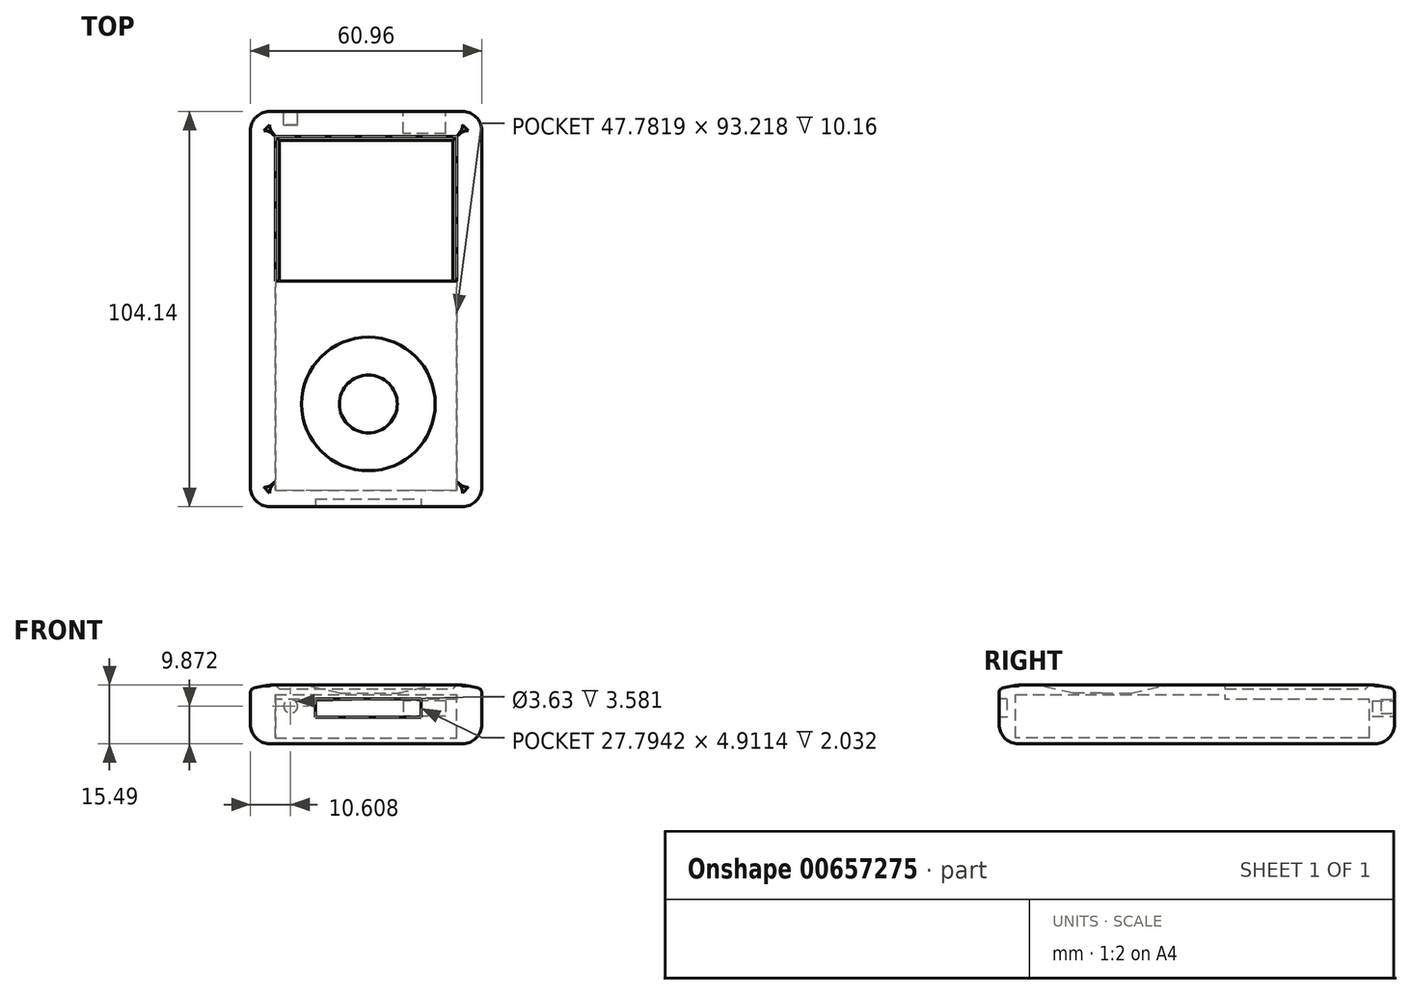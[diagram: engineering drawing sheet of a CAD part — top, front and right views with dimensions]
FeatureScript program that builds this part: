
annotation { "Feature Type Name" : "Feature", "Feature Type Description" : "" }
export const myFeature = defineFeature(function(context is Context, id is Id, definition is map)
    precondition{}
    {
        {
            var Q0;
            Q0=qCreatedBy(makeId("Top.planeOp"),FACE);
            var sketch = newSketch(context, id + "F0", { "sketchPlane" : qUnion([Q0])});
            skLineSegment(sketch, "E0.bottom", {"start": v(-31.08, 69.47) * mm, "end": v(29.88, 69.47) * mm});
            skLineSegment(sketch, "E0.top", {"start": v(-31.08, -34.67) * mm, "end": v(29.88, -34.67) * mm});
            skLineSegment(sketch, "E0.left", {"start": v(-31.08, 69.47) * mm, "end": v(-31.08, -34.67) * mm});
            skLineSegment(sketch, "E0.right", {"start": v(29.88, 69.47) * mm, "end": v(29.88, -34.67) * mm});
            skSolve(sketch);
        }
        {
            var Q0;
            Q0=makeQuery(id+"F0.imprint","IMPRINT",FACE,{"disambiguationData":[TD([[makeQuery(id+"F0.imprint","IMPRINT",EDGE,{"derivedFrom":sQuery(id+"F0.wireOp",EDGE,"E0.bottom")}),-1.0]])]});
            extrude(context, id + "F1", {"entities" : qUnion([Q0]), "depth" : 15.24 * mm, "offsetDistance" : 25.4 * mm});
        }
        {
            var Q0;
            Q0=makeQuery(id+"F1.opExtrude","SWEPT_EDGE",EDGE,{"disambiguationData":[OSD([sQuery(id+"F0.wireOp",EDGE,"E0.bottom"),sQuery(id+"F0.wireOp",EDGE,"E0.right")])]});
            var Q1;
            Q1=makeQuery(id+"F1.opExtrude","SWEPT_EDGE",EDGE,{"disambiguationData":[OSD([sQuery(id+"F0.wireOp",EDGE,"E0.bottom"),sQuery(id+"F0.wireOp",EDGE,"E0.left")])]});
            var Q2;
            Q2=makeQuery(id+"F1.opExtrude","SWEPT_EDGE",EDGE,{"disambiguationData":[OSD([sQuery(id+"F0.wireOp",EDGE,"E0.top"),sQuery(id+"F0.wireOp",EDGE,"E0.right")])]});
            var Q3;
            Q3=makeQuery(id+"F1.opExtrude","SWEPT_EDGE",EDGE,{"disambiguationData":[OSD([sQuery(id+"F0.wireOp",EDGE,"E0.top"),sQuery(id+"F0.wireOp",EDGE,"E0.left")])]});
            fillet(context, id + "F2", {"entities" : qUnion([Q0, Q1, Q2, Q3]), "radius" : 5.08 * mm, "tangentPropagation" : true, "allowEdgeOverflow" : false});
        }
        {
            var Q0;
            Q0=makeQuery(id+"FoFVW0M2sbFO0MS_1.boolean.opBoolean","SPLIT",FACE,{"disambiguationData":[TD([makeQuery(id+"FoFVW0M2sbFO0MS_1.opExtrude","SWEPT_FACE",FACE,{"disambiguationData":[OSD([sQuery(id+"FxMzDEaBXAed3TF_1.wireOp",EDGE,"OPwGTAcq-u0Vr-5pPN-neVn-fGhoZMYUlgc0")])]})])],"derivedFrom":makeQuery(id+"F1.opExtrude","CAP_FACE",FACE,{"disambiguationData":[OSD([sQuery(id+"F0.wireOp",EDGE,"E0.bottom"),sQuery(id+"F0.wireOp",EDGE,"E0.top"),sQuery(id+"F0.wireOp",EDGE,"E0.left"),sQuery(id+"F0.wireOp",EDGE,"E0.right")])],"isStart":false})});
            extrude(context, id + "F3", {"entities" : qUnion([Q0]), "operationType" : NewBodyOperationType.ADD, "depth" : 0.25 * mm, "offsetDistance" : 25.4 * mm});
        }
        {
            var Q0;
            Q0=makeQuery(id+"F1.opExtrude","CAP_EDGE",EDGE,{"disambiguationData":[OSD([sQuery(id+"F0.wireOp",EDGE,"E0.right")])],"isStart":true});
            var Q1;
            Q1=makeQuery(id+"F1.opExtrude","CAP_EDGE",EDGE,{"disambiguationData":[OSD([sQuery(id+"F0.wireOp",EDGE,"E0.bottom")])],"isStart":true});
            var Q2;
            Q2=makeQuery(id+"F1.opExtrude","CAP_EDGE",EDGE,{"disambiguationData":[OSD([sQuery(id+"F0.wireOp",EDGE,"E0.left")])],"isStart":true});
            var Q3;
            Q3=makeQuery(id+"F1.opExtrude","CAP_EDGE",EDGE,{"disambiguationData":[OSD([sQuery(id+"F0.wireOp",EDGE,"E0.top")])],"isStart":true});
            var Q4;
            {var subQ0=sQuery(id+"F0.wireOp",EDGE,"E0.left");var subQ1=sQuery(id+"F0.wireOp",EDGE,"E0.top");Q4=makeQuery(id+"F2.opFillet","BLEND_EDGE",EDGE,{"blendedFrom":[makeQuery(id+"F1.opExtrude","SWEPT_EDGE",EDGE,{"disambiguationData":[OSD([subQ1,subQ0])]}),makeQuery(id+"F1.opExtrude","CAP_FACE",FACE,{"disambiguationData":[OSD([sQuery(id+"F0.wireOp",EDGE,"E0.bottom"),subQ1,subQ0,sQuery(id+"F0.wireOp",EDGE,"E0.right")])],"isStart":true})],"blendedInto":[makeQuery(id+"F1.opExtrude","CAP_FACE",FACE,{"disambiguationData":[OSD([sQuery(id+"F0.wireOp",EDGE,"E0.bottom"),subQ1,subQ0,sQuery(id+"F0.wireOp",EDGE,"E0.right")])],"isStart":true})]});}
            var Q5;
            {var subQ0=sQuery(id+"F0.wireOp",EDGE,"E0.right");var subQ1=sQuery(id+"F0.wireOp",EDGE,"E0.top");Q5=makeQuery(id+"F2.opFillet","BLEND_EDGE",EDGE,{"blendedFrom":[makeQuery(id+"F1.opExtrude","SWEPT_EDGE",EDGE,{"disambiguationData":[OSD([subQ1,subQ0])]}),makeQuery(id+"F1.opExtrude","CAP_FACE",FACE,{"disambiguationData":[OSD([sQuery(id+"F0.wireOp",EDGE,"E0.bottom"),subQ1,sQuery(id+"F0.wireOp",EDGE,"E0.left"),subQ0])],"isStart":true})],"blendedInto":[makeQuery(id+"F1.opExtrude","CAP_FACE",FACE,{"disambiguationData":[OSD([sQuery(id+"F0.wireOp",EDGE,"E0.bottom"),subQ1,sQuery(id+"F0.wireOp",EDGE,"E0.left"),subQ0])],"isStart":true})]});}
            var Q6;
            {var subQ0=sQuery(id+"F0.wireOp",EDGE,"E0.left");var subQ1=sQuery(id+"F0.wireOp",EDGE,"E0.bottom");Q6=makeQuery(id+"F2.opFillet","BLEND_EDGE",EDGE,{"blendedFrom":[makeQuery(id+"F1.opExtrude","SWEPT_EDGE",EDGE,{"disambiguationData":[OSD([subQ1,subQ0])]}),makeQuery(id+"F1.opExtrude","CAP_FACE",FACE,{"disambiguationData":[OSD([subQ1,sQuery(id+"F0.wireOp",EDGE,"E0.top"),subQ0,sQuery(id+"F0.wireOp",EDGE,"E0.right")])],"isStart":true})],"blendedInto":[makeQuery(id+"F1.opExtrude","CAP_FACE",FACE,{"disambiguationData":[OSD([subQ1,sQuery(id+"F0.wireOp",EDGE,"E0.top"),subQ0,sQuery(id+"F0.wireOp",EDGE,"E0.right")])],"isStart":true})]});}
            var Q7;
            {var subQ0=sQuery(id+"F0.wireOp",EDGE,"E0.right");var subQ1=sQuery(id+"F0.wireOp",EDGE,"E0.bottom");Q7=makeQuery(id+"F2.opFillet","BLEND_EDGE",EDGE,{"blendedFrom":[makeQuery(id+"F1.opExtrude","SWEPT_EDGE",EDGE,{"disambiguationData":[OSD([subQ1,subQ0])]}),makeQuery(id+"F1.opExtrude","CAP_FACE",FACE,{"disambiguationData":[OSD([subQ1,sQuery(id+"F0.wireOp",EDGE,"E0.top"),sQuery(id+"F0.wireOp",EDGE,"E0.left"),subQ0])],"isStart":true})],"blendedInto":[makeQuery(id+"F1.opExtrude","CAP_FACE",FACE,{"disambiguationData":[OSD([subQ1,sQuery(id+"F0.wireOp",EDGE,"E0.top"),sQuery(id+"F0.wireOp",EDGE,"E0.left"),subQ0])],"isStart":true})]});}
            fillet(context, id + "F4", {"entities" : qUnion([Q0, Q1, Q2, Q3, Q4, Q5, Q6, Q7]), "radius" : 5.08 * mm, "tangentPropagation" : true, "allowEdgeOverflow" : false});
        }
        {
            var Q0;
            Q0=qCreatedBy(makeId("Right.planeOp"),FACE);
            var sketch = newSketch(context, id + "F5", { "sketchPlane" : qUnion([Q0])});
            skLineSegment(sketch, "E1", {"start": v(-7.62, 15.53) * mm, "end": v(-7.62, 13.3) * mm});
            skLineSegment(sketch, "E2", {"start": v(-7.62, 13.3) * mm, "end": v(0, 13.3) * mm});
            skLineSegment(sketch, "E3", {"start": v(0, 13.3) * mm, "end": v(10.16, 15.53) * mm});
            skLineSegment(sketch, "E4", {"start": v(10.16, 15.53) * mm, "end": v(-7.62, 15.53) * mm});
            skSolve(sketch);
        }
        {
            var Q0;
            Q0 = qSketchRegion(id + "F5", true);
            var Q1;
            Q1=sQuery(id+"F5.wireOp",EDGE,"E1");
            revolve(context, id + "F6", {"operationType" : NewBodyOperationType.REMOVE, "entities" : qUnion([Q0]), "axis" : qUnion([Q1]), "revolveType" : RevolveType.FULL, "oppositeDirection" : true});
        }
        {
            var Q0;
            Q0=makeQuery(id+"F3.opExtrude","CAP_EDGE",EDGE,{"disambiguationData":[OSD([sQuery(id+"F0.wireOp",EDGE,"E0.left")])],"isStart":false});
            chamfer(context, id + "F7", {"entities" : qUnion([Q0]), "chamferType" : ChamferType.TWO_OFFSETS, "width1" : 5.08 * mm, "oppositeDirection" : false, "width2" : 1.02 * mm, "tangentPropagation" : true});
        }
        {
            var Q0;
            {var subQ0=sQuery(id+"F0.wireOp",EDGE,"E0.left");Q0=makeQuery(id+"F7.opChamfer","BLEND_EDGE",EDGE,{"blendedFrom":[makeQuery(id+"F3.opExtrude","CAP_EDGE",EDGE,{"disambiguationData":[OSD([subQ0])],"isStart":false}),makeQuery(id+"F3.opExtrude","CAP_FACE",FACE,{"disambiguationData":[OSD([sQuery(id+"F0.wireOp",EDGE,"E0.bottom"),sQuery(id+"F0.wireOp",EDGE,"E0.top"),subQ0,sQuery(id+"F0.wireOp",EDGE,"E0.right")])],"isStart":false})],"blendedInto":[makeQuery(id+"F3.opExtrude","CAP_FACE",FACE,{"disambiguationData":[OSD([sQuery(id+"F0.wireOp",EDGE,"E0.bottom"),sQuery(id+"F0.wireOp",EDGE,"E0.top"),subQ0,sQuery(id+"F0.wireOp",EDGE,"E0.right")])],"isStart":false})]});}
            var Q1;
            {var subQ0=sQuery(id+"F0.wireOp",EDGE,"E0.top");Q1=makeQuery(id+"F7.opChamfer","BLEND_EDGE",EDGE,{"blendedFrom":[makeQuery(id+"F3.opExtrude","CAP_EDGE",EDGE,{"disambiguationData":[OSD([subQ0])],"isStart":false}),makeQuery(id+"F3.opExtrude","CAP_FACE",FACE,{"disambiguationData":[OSD([sQuery(id+"F0.wireOp",EDGE,"E0.bottom"),subQ0,sQuery(id+"F0.wireOp",EDGE,"E0.left"),sQuery(id+"F0.wireOp",EDGE,"E0.right")])],"isStart":false})],"blendedInto":[makeQuery(id+"F3.opExtrude","CAP_FACE",FACE,{"disambiguationData":[OSD([sQuery(id+"F0.wireOp",EDGE,"E0.bottom"),subQ0,sQuery(id+"F0.wireOp",EDGE,"E0.left"),sQuery(id+"F0.wireOp",EDGE,"E0.right")])],"isStart":false})]});}
            var Q2;
            {var subQ0=sQuery(id+"F0.wireOp",EDGE,"E0.right");Q2=makeQuery(id+"F7.opChamfer","BLEND_EDGE",EDGE,{"blendedFrom":[makeQuery(id+"F3.opExtrude","CAP_EDGE",EDGE,{"disambiguationData":[OSD([subQ0])],"isStart":false}),makeQuery(id+"F3.opExtrude","CAP_FACE",FACE,{"disambiguationData":[OSD([sQuery(id+"F0.wireOp",EDGE,"E0.bottom"),sQuery(id+"F0.wireOp",EDGE,"E0.top"),sQuery(id+"F0.wireOp",EDGE,"E0.left"),subQ0])],"isStart":false})],"blendedInto":[makeQuery(id+"F3.opExtrude","CAP_FACE",FACE,{"disambiguationData":[OSD([sQuery(id+"F0.wireOp",EDGE,"E0.bottom"),sQuery(id+"F0.wireOp",EDGE,"E0.top"),sQuery(id+"F0.wireOp",EDGE,"E0.left"),subQ0])],"isStart":false})]});}
            var Q3;
            {var subQ0=sQuery(id+"F0.wireOp",EDGE,"E0.bottom");Q3=makeQuery(id+"F7.opChamfer","BLEND_EDGE",EDGE,{"blendedFrom":[makeQuery(id+"F3.opExtrude","CAP_EDGE",EDGE,{"disambiguationData":[OSD([subQ0])],"isStart":false}),makeQuery(id+"F3.opExtrude","CAP_FACE",FACE,{"disambiguationData":[OSD([subQ0,sQuery(id+"F0.wireOp",EDGE,"E0.top"),sQuery(id+"F0.wireOp",EDGE,"E0.left"),sQuery(id+"F0.wireOp",EDGE,"E0.right")])],"isStart":false})],"blendedInto":[makeQuery(id+"F3.opExtrude","CAP_FACE",FACE,{"disambiguationData":[OSD([subQ0,sQuery(id+"F0.wireOp",EDGE,"E0.top"),sQuery(id+"F0.wireOp",EDGE,"E0.left"),sQuery(id+"F0.wireOp",EDGE,"E0.right")])],"isStart":false})]});}
            fillet(context, id + "F8", {"entities" : qUnion([Q0, Q1, Q2, Q3]), "radius" : 15.24 * mm, "tangentPropagation" : true, "allowEdgeOverflow" : false});
        }
        {
            var Q0;
            Q0=makeQuery(id+"F3.opExtrude","CAP_FACE",FACE,{"disambiguationData":[OSD([sQuery(id+"F0.wireOp",EDGE,"E0.bottom"),sQuery(id+"F0.wireOp",EDGE,"E0.top"),sQuery(id+"F0.wireOp",EDGE,"E0.left"),sQuery(id+"F0.wireOp",EDGE,"E0.right")])],"isStart":false});
            var sketch = newSketch(context, id + "F9", { "sketchPlane" : qUnion([Q0])});
            skLineSegment(sketch, "E5.bottom", {"start": v(-24.5, 62.88) * mm, "end": v(23.29, 62.88) * mm});
            skLineSegment(sketch, "E5.top", {"start": v(-24.5, 24.78) * mm, "end": v(23.29, 24.78) * mm});
            skLineSegment(sketch, "E5.left", {"start": v(-24.5, 62.88) * mm, "end": v(-24.5, 24.78) * mm});
            skLineSegment(sketch, "E5.right", {"start": v(23.29, 62.88) * mm, "end": v(23.29, 24.78) * mm});
            skSolve(sketch);
        }
        {
            var Q0;
            Q0 = qSketchRegion(id + "F9", true);
            extrude(context, id + "F10", {"entities" : qUnion([Q0]), "operationType" : NewBodyOperationType.REMOVE, "oppositeDirection" : true, "depth" : 13.97 * mm, "offsetDistance" : 25.4 * mm});
        }
        {
            var Q0;
            Q0=makeQuery(id+"F10.boolean.opBoolean","COPY",FACE,{"derivedFrom":makeQuery(id+"F10.opExtrude","SWEPT_FACE",FACE,{"disambiguationData":[OSD([sQuery(id+"F9.wireOp",EDGE,"E5.top")])]})});
            var sketch = newSketch(context, id + "F11", { "sketchPlane" : qUnion([Q0])});
            skLineSegment(sketch, "E6.0", {"start": v(24.5, 1.52) * mm, "end": v(-23.29, 1.52) * mm});
            skLineSegment(sketch, "E7", {"start": v(-23.29, 1.52) * mm, "end": v(-23.29, 12.95) * mm});
            skLineSegment(sketch, "E8", {"start": v(-23.29, 12.95) * mm, "end": v(24.5, 12.95) * mm});
            skLineSegment(sketch, "E9", {"start": v(24.5, 12.95) * mm, "end": v(24.5, 1.52) * mm});
            skSolve(sketch);
        }
        {
            var Q0;
            Q0=makeQuery(id+"F11.imprint","IMPRINT",FACE,{"disambiguationData":[TD([[makeQuery(id+"F11.imprint","IMPRINT",EDGE,{"derivedFrom":sQuery(id+"F11.wireOp",EDGE,"E6.0")}),-1.0]])]});
            extrude(context, id + "F12", {"entities" : qUnion([Q0]), "operationType" : NewBodyOperationType.REMOVE, "oppositeDirection" : true, "depth" : 55.12 * mm, "offsetDistance" : 25.4 * mm});
        }
        {
            var Q0;
            Q0=makeQuery(id+"F12.boolean.opBoolean","MERGE",FACE,{"derivedFrom":[makeQuery(id+"F10.boolean.opBoolean","COPY",FACE,{"derivedFrom":makeQuery(id+"F10.opExtrude","CAP_FACE",FACE,{"disambiguationData":[OSD([sQuery(id+"F9.wireOp",EDGE,"E5.bottom"),sQuery(id+"F9.wireOp",EDGE,"E5.top"),sQuery(id+"F9.wireOp",EDGE,"E5.left"),sQuery(id+"F9.wireOp",EDGE,"E5.right")])],"isStart":false})}),makeQuery(id+"F12.opExtrude","SWEPT_FACE",FACE,{"disambiguationData":[OSD([sQuery(id+"F11.wireOp",EDGE,"E6.0")])]})]});
            var sketch = newSketch(context, id + "F13", { "sketchPlane" : qUnion([Q0])});
            skLineSegment(sketch, "E10.bottom", {"start": v(23.29, 62.88) * mm, "end": v(-24.5, 62.88) * mm});
            skLineSegment(sketch, "E10.top", {"start": v(23.29, 24.78) * mm, "end": v(-24.5, 24.78) * mm});
            skLineSegment(sketch, "E10.left", {"start": v(23.29, 62.88) * mm, "end": v(23.29, 24.78) * mm});
            skLineSegment(sketch, "E10.right", {"start": v(-24.5, 62.88) * mm, "end": v(-24.5, 24.78) * mm});
            skSolve(sketch);
        }
        {
            var Q0;
            Q0=makeQuery(id+"F13.imprint","IMPRINT",FACE,{"disambiguationData":[TD([[makeQuery(id+"F13.imprint","IMPRINT",EDGE,{"derivedFrom":sQuery(id+"F13.wireOp",EDGE,"E10.bottom")}),1.0]])]});
            extrude(context, id + "F14", {"entities" : qUnion([Q0]), "operationType" : NewBodyOperationType.ADD, "depth" : 12.95 * mm, "offsetDistance" : 25.4 * mm, "hasSecondDirection" : true, "secondDirectionOppositeDirection" : false, "secondDirectionDepth" : 10.16 * mm});
        }
        {
            var Q0;
            {var subQ0=sQuery(id+"F0.wireOp",EDGE,"E0.left");Q0=makeQuery(id+"F7.opChamfer","BLEND_EDGE",EDGE,{"blendedFrom":[makeQuery(id+"F3.opExtrude","CAP_EDGE",EDGE,{"disambiguationData":[OSD([subQ0])],"isStart":false}),makeQuery(id+"F3.boolean.opBoolean","MERGE",FACE,{"derivedFrom":[makeQuery(id+"F1.opExtrude","SWEPT_FACE",FACE,{"disambiguationData":[OSD([subQ0])]}),makeQuery(id+"F3.opExtrude","SWEPT_FACE",FACE,{"disambiguationData":[OSD([subQ0])]})]})],"blendedInto":[makeQuery(id+"F3.boolean.opBoolean","MERGE",FACE,{"derivedFrom":[makeQuery(id+"F1.opExtrude","SWEPT_FACE",FACE,{"disambiguationData":[OSD([subQ0])]}),makeQuery(id+"F3.opExtrude","SWEPT_FACE",FACE,{"disambiguationData":[OSD([subQ0])]})]})]});}
            var Q1;
            {var subQ0=sQuery(id+"F0.wireOp",EDGE,"E0.right");var subQ1=sQuery(id+"F0.wireOp",EDGE,"E0.left");var subQ2=sQuery(id+"F0.wireOp",EDGE,"E0.top");var subQ3=sQuery(id+"F0.wireOp",EDGE,"E0.bottom");var subQ4=makeQuery(id+"F2.opFillet","BLEND_EDGE",EDGE,{"blendedFrom":[makeQuery(id+"F1.opExtrude","SWEPT_EDGE",EDGE,{"disambiguationData":[OSD([subQ3,subQ1])]}),makeQuery(id+"F1.opExtrude","CAP_FACE",FACE,{"disambiguationData":[OSD([subQ3,subQ2,subQ1,subQ0])],"isStart":false})],"blendedInto":[makeQuery(id+"F1.opExtrude","CAP_FACE",FACE,{"disambiguationData":[OSD([subQ3,subQ2,subQ1,subQ0])],"isStart":false})]});Q1=makeQuery(id+"F7.opChamfer","BLEND_EDGE",EDGE,{"blendedFrom":[makeQuery(id+"F3.opExtrude","CAP_EDGE",EDGE,{"disambiguationData":[OSD([subQ3,subQ2,subQ1,subQ0]),TDD([subQ4])],"isStart":false}),makeQuery(id+"F3.boolean.opBoolean","MERGE",FACE,{"derivedFrom":[makeQuery(id+"F2.opFillet","BLEND_FACE",FACE,{"disambiguationData":[OSD([subQ3,subQ1])]}),makeQuery(id+"F3.opExtrude","SWEPT_FACE",FACE,{"disambiguationData":[OSD([subQ3,subQ2,subQ1,subQ0]),TDD([subQ4])]})]})],"blendedInto":[makeQuery(id+"F3.boolean.opBoolean","MERGE",FACE,{"derivedFrom":[makeQuery(id+"F2.opFillet","BLEND_FACE",FACE,{"disambiguationData":[OSD([subQ3,subQ1])]}),makeQuery(id+"F3.opExtrude","SWEPT_FACE",FACE,{"disambiguationData":[OSD([subQ3,subQ2,subQ1,subQ0]),TDD([subQ4])]})]})]});}
            var Q2;
            {var subQ0=sQuery(id+"F0.wireOp",EDGE,"E0.bottom");Q2=makeQuery(id+"F7.opChamfer","BLEND_EDGE",EDGE,{"blendedFrom":[makeQuery(id+"F3.opExtrude","CAP_EDGE",EDGE,{"disambiguationData":[OSD([subQ0])],"isStart":false}),makeQuery(id+"F3.boolean.opBoolean","MERGE",FACE,{"derivedFrom":[makeQuery(id+"F1.opExtrude","SWEPT_FACE",FACE,{"disambiguationData":[OSD([subQ0])]}),makeQuery(id+"F3.opExtrude","SWEPT_FACE",FACE,{"disambiguationData":[OSD([subQ0])]})]})],"blendedInto":[makeQuery(id+"F3.boolean.opBoolean","MERGE",FACE,{"derivedFrom":[makeQuery(id+"F1.opExtrude","SWEPT_FACE",FACE,{"disambiguationData":[OSD([subQ0])]}),makeQuery(id+"F3.opExtrude","SWEPT_FACE",FACE,{"disambiguationData":[OSD([subQ0])]})]})]});}
            var Q3;
            {var subQ0=sQuery(id+"F0.wireOp",EDGE,"E0.right");var subQ1=sQuery(id+"F0.wireOp",EDGE,"E0.left");var subQ2=sQuery(id+"F0.wireOp",EDGE,"E0.top");var subQ3=sQuery(id+"F0.wireOp",EDGE,"E0.bottom");var subQ4=makeQuery(id+"F2.opFillet","BLEND_EDGE",EDGE,{"blendedFrom":[makeQuery(id+"F1.opExtrude","SWEPT_EDGE",EDGE,{"disambiguationData":[OSD([subQ2,subQ1])]}),makeQuery(id+"F1.opExtrude","CAP_FACE",FACE,{"disambiguationData":[OSD([subQ3,subQ2,subQ1,subQ0])],"isStart":false})],"blendedInto":[makeQuery(id+"F1.opExtrude","CAP_FACE",FACE,{"disambiguationData":[OSD([subQ3,subQ2,subQ1,subQ0])],"isStart":false})]});Q3=makeQuery(id+"F7.opChamfer","BLEND_EDGE",EDGE,{"blendedFrom":[makeQuery(id+"F3.opExtrude","CAP_EDGE",EDGE,{"disambiguationData":[OSD([subQ3,subQ2,subQ1,subQ0]),TDD([subQ4])],"isStart":false}),makeQuery(id+"F3.boolean.opBoolean","MERGE",FACE,{"derivedFrom":[makeQuery(id+"F2.opFillet","BLEND_FACE",FACE,{"disambiguationData":[OSD([subQ2,subQ1])]}),makeQuery(id+"F3.opExtrude","SWEPT_FACE",FACE,{"disambiguationData":[OSD([subQ3,subQ2,subQ1,subQ0]),TDD([subQ4])]})]})],"blendedInto":[makeQuery(id+"F3.boolean.opBoolean","MERGE",FACE,{"derivedFrom":[makeQuery(id+"F2.opFillet","BLEND_FACE",FACE,{"disambiguationData":[OSD([subQ2,subQ1])]}),makeQuery(id+"F3.opExtrude","SWEPT_FACE",FACE,{"disambiguationData":[OSD([subQ3,subQ2,subQ1,subQ0]),TDD([subQ4])]})]})]});}
            var Q4;
            {var subQ0=sQuery(id+"F0.wireOp",EDGE,"E0.top");Q4=makeQuery(id+"F7.opChamfer","BLEND_EDGE",EDGE,{"blendedFrom":[makeQuery(id+"F3.opExtrude","CAP_EDGE",EDGE,{"disambiguationData":[OSD([subQ0])],"isStart":false}),makeQuery(id+"F3.boolean.opBoolean","MERGE",FACE,{"derivedFrom":[makeQuery(id+"F1.opExtrude","SWEPT_FACE",FACE,{"disambiguationData":[OSD([subQ0])]}),makeQuery(id+"F3.opExtrude","SWEPT_FACE",FACE,{"disambiguationData":[OSD([subQ0])]})]})],"blendedInto":[makeQuery(id+"F3.boolean.opBoolean","MERGE",FACE,{"derivedFrom":[makeQuery(id+"F1.opExtrude","SWEPT_FACE",FACE,{"disambiguationData":[OSD([subQ0])]}),makeQuery(id+"F3.opExtrude","SWEPT_FACE",FACE,{"disambiguationData":[OSD([subQ0])]})]})]});}
            var Q5;
            {var subQ0=sQuery(id+"F0.wireOp",EDGE,"E0.right");var subQ1=sQuery(id+"F0.wireOp",EDGE,"E0.left");var subQ2=sQuery(id+"F0.wireOp",EDGE,"E0.top");var subQ3=sQuery(id+"F0.wireOp",EDGE,"E0.bottom");var subQ4=makeQuery(id+"F2.opFillet","BLEND_EDGE",EDGE,{"blendedFrom":[makeQuery(id+"F1.opExtrude","SWEPT_EDGE",EDGE,{"disambiguationData":[OSD([subQ2,subQ0])]}),makeQuery(id+"F1.opExtrude","CAP_FACE",FACE,{"disambiguationData":[OSD([subQ3,subQ2,subQ1,subQ0])],"isStart":false})],"blendedInto":[makeQuery(id+"F1.opExtrude","CAP_FACE",FACE,{"disambiguationData":[OSD([subQ3,subQ2,subQ1,subQ0])],"isStart":false})]});Q5=makeQuery(id+"F7.opChamfer","BLEND_EDGE",EDGE,{"blendedFrom":[makeQuery(id+"F3.opExtrude","CAP_EDGE",EDGE,{"disambiguationData":[OSD([subQ3,subQ2,subQ1,subQ0]),TDD([subQ4])],"isStart":false}),makeQuery(id+"F3.boolean.opBoolean","MERGE",FACE,{"derivedFrom":[makeQuery(id+"F2.opFillet","BLEND_FACE",FACE,{"disambiguationData":[OSD([subQ2,subQ0])]}),makeQuery(id+"F3.opExtrude","SWEPT_FACE",FACE,{"disambiguationData":[OSD([subQ3,subQ2,subQ1,subQ0]),TDD([subQ4])]})]})],"blendedInto":[makeQuery(id+"F3.boolean.opBoolean","MERGE",FACE,{"derivedFrom":[makeQuery(id+"F2.opFillet","BLEND_FACE",FACE,{"disambiguationData":[OSD([subQ2,subQ0])]}),makeQuery(id+"F3.opExtrude","SWEPT_FACE",FACE,{"disambiguationData":[OSD([subQ3,subQ2,subQ1,subQ0]),TDD([subQ4])]})]})]});}
            var Q6;
            {var subQ0=sQuery(id+"F0.wireOp",EDGE,"E0.right");Q6=makeQuery(id+"F7.opChamfer","BLEND_EDGE",EDGE,{"blendedFrom":[makeQuery(id+"F3.opExtrude","CAP_EDGE",EDGE,{"disambiguationData":[OSD([subQ0])],"isStart":false}),makeQuery(id+"F3.boolean.opBoolean","MERGE",FACE,{"derivedFrom":[makeQuery(id+"F1.opExtrude","SWEPT_FACE",FACE,{"disambiguationData":[OSD([subQ0])]}),makeQuery(id+"F3.opExtrude","SWEPT_FACE",FACE,{"disambiguationData":[OSD([subQ0])]})]})],"blendedInto":[makeQuery(id+"F3.boolean.opBoolean","MERGE",FACE,{"derivedFrom":[makeQuery(id+"F1.opExtrude","SWEPT_FACE",FACE,{"disambiguationData":[OSD([subQ0])]}),makeQuery(id+"F3.opExtrude","SWEPT_FACE",FACE,{"disambiguationData":[OSD([subQ0])]})]})]});}
            var Q7;
            {var subQ0=sQuery(id+"F0.wireOp",EDGE,"E0.right");var subQ1=sQuery(id+"F0.wireOp",EDGE,"E0.left");var subQ2=sQuery(id+"F0.wireOp",EDGE,"E0.top");var subQ3=sQuery(id+"F0.wireOp",EDGE,"E0.bottom");var subQ4=makeQuery(id+"F2.opFillet","BLEND_EDGE",EDGE,{"blendedFrom":[makeQuery(id+"F1.opExtrude","SWEPT_EDGE",EDGE,{"disambiguationData":[OSD([subQ3,subQ0])]}),makeQuery(id+"F1.opExtrude","CAP_FACE",FACE,{"disambiguationData":[OSD([subQ3,subQ2,subQ1,subQ0])],"isStart":false})],"blendedInto":[makeQuery(id+"F1.opExtrude","CAP_FACE",FACE,{"disambiguationData":[OSD([subQ3,subQ2,subQ1,subQ0])],"isStart":false})]});Q7=makeQuery(id+"F7.opChamfer","BLEND_EDGE",EDGE,{"blendedFrom":[makeQuery(id+"F3.opExtrude","CAP_EDGE",EDGE,{"disambiguationData":[OSD([subQ3,subQ2,subQ1,subQ0]),TDD([subQ4])],"isStart":false}),makeQuery(id+"F3.boolean.opBoolean","MERGE",FACE,{"derivedFrom":[makeQuery(id+"F2.opFillet","BLEND_FACE",FACE,{"disambiguationData":[OSD([subQ3,subQ0])]}),makeQuery(id+"F3.opExtrude","SWEPT_FACE",FACE,{"disambiguationData":[OSD([subQ3,subQ2,subQ1,subQ0]),TDD([subQ4])]})]})],"blendedInto":[makeQuery(id+"F3.boolean.opBoolean","MERGE",FACE,{"derivedFrom":[makeQuery(id+"F2.opFillet","BLEND_FACE",FACE,{"disambiguationData":[OSD([subQ3,subQ0])]}),makeQuery(id+"F3.opExtrude","SWEPT_FACE",FACE,{"disambiguationData":[OSD([subQ3,subQ2,subQ1,subQ0]),TDD([subQ4])]})]})]});}
            fillet(context, id + "F15", {"entities" : qUnion([Q0, Q1, Q2, Q3, Q4, Q5, Q6, Q7]), "radius" : 1.27 * mm, "tangentPropagation" : true, "allowEdgeOverflow" : false});
        }
        {
            var Q0;
            {var subQ0=sQuery(id+"F0.wireOp",EDGE,"E0.top");Q0=makeQuery(id+"F3.boolean.opBoolean","MERGE",FACE,{"derivedFrom":[makeQuery(id+"F1.opExtrude","SWEPT_FACE",FACE,{"disambiguationData":[OSD([subQ0])]}),makeQuery(id+"F3.opExtrude","SWEPT_FACE",FACE,{"disambiguationData":[OSD([subQ0])]})]});}
            var sketch = newSketch(context, id + "F16", { "sketchPlane" : qUnion([Q0])});
            skLineSegment(sketch, "E11.bottom", {"start": v(-13.9, 11.83) * mm, "end": v(13.9, 11.83) * mm});
            skLineSegment(sketch, "E11.top", {"start": v(-13.9, 6.91) * mm, "end": v(13.9, 6.91) * mm});
            skLineSegment(sketch, "E11.left", {"start": v(-13.9, 11.83) * mm, "end": v(-13.9, 6.91) * mm});
            skLineSegment(sketch, "E11.right", {"start": v(13.9, 11.83) * mm, "end": v(13.9, 6.91) * mm});
            skPoint(sketch, "E11.middle", {"position": v(0, 9.37) * mm});
            skSolve(sketch);
        }
        {
            var Q0;
            Q0=makeQuery(id+"F16.imprint","IMPRINT",FACE,{"disambiguationData":[TD([[makeQuery(id+"F16.imprint","IMPRINT",EDGE,{"derivedFrom":sQuery(id+"F16.wireOp",EDGE,"E11.bottom")}),-1.0]])]});
            extrude(context, id + "F17", {"entities" : qUnion([Q0]), "operationType" : NewBodyOperationType.REMOVE, "oppositeDirection" : true, "depth" : 2.03 * mm, "offsetDistance" : 25.4 * mm});
        }
        {
            var Q0;
            {var subQ0=sQuery(id+"F0.wireOp",EDGE,"E0.bottom");Q0=makeQuery(id+"F3.boolean.opBoolean","MERGE",FACE,{"derivedFrom":[makeQuery(id+"F1.opExtrude","SWEPT_FACE",FACE,{"disambiguationData":[OSD([subQ0])]}),makeQuery(id+"F3.opExtrude","SWEPT_FACE",FACE,{"disambiguationData":[OSD([subQ0])]})]});}
            var sketch = newSketch(context, id + "F18", { "sketchPlane" : qUnion([Q0])});
            skLineSegment(sketch, "E12.bottom", {"start": v(-20.38, 11.32) * mm, "end": v(-9.22, 11.32) * mm});
            skLineSegment(sketch, "E12.top", {"start": v(-20.38, 7.2) * mm, "end": v(-9.22, 7.2) * mm});
            skLineSegment(sketch, "E12.left", {"start": v(-20.38, 11.32) * mm, "end": v(-20.38, 7.2) * mm});
            skLineSegment(sketch, "E12.right", {"start": v(-9.22, 11.32) * mm, "end": v(-9.22, 7.2) * mm});
            skPoint(sketch, "E12.middle", {"position": v(-14.8, 9.26) * mm});
            skPoint(sketch, "E12.middle.positionSnap0", {"position": v(-24.8, 9.26) * mm});
            skPoint(sketch, "E12.centerSnap0", {"position": v(-24.8, 9.26) * mm});
            skSolve(sketch);
        }
        {
            var Q0;
            Q0=makeQuery(id+"F18.imprint","IMPRINT",FACE,{"disambiguationData":[TD([[makeQuery(id+"F18.imprint","IMPRINT",EDGE,{"derivedFrom":sQuery(id+"F18.wireOp",EDGE,"E12.bottom")}),1.0]])]});
            var sketch = newSketch(context, id + "F19", { "sketchPlane" : qUnion([Q0])});
            skCircle(sketch, "E13", {"center": v(20.47, 9.87) * mm, "radius": 1.82 * mm});
            skSolve(sketch);
        }
        {
            var Q0;
            Q0=makeQuery(id+"F18.imprint","IMPRINT",FACE,{"disambiguationData":[TD([[makeQuery(id+"F18.imprint","IMPRINT",EDGE,{"derivedFrom":sQuery(id+"F18.wireOp",EDGE,"E12.bottom")}),-1.0]])]});
            extrude(context, id + "F20", {"entities" : qUnion([Q0]), "operationType" : NewBodyOperationType.REMOVE, "oppositeDirection" : true, "depth" : 5.84 * mm, "offsetDistance" : 25.4 * mm});
        }
        {
            var Q0;
            Q0=makeQuery(id+"F19.imprint","IMPRINT",FACE,{"disambiguationData":[TD([[makeQuery(id+"F19.imprint","IMPRINT",EDGE,{"derivedFrom":sQuery(id+"F19.wireOp",EDGE,"E13")}),1.0]])]});
            extrude(context, id + "F21", {"entities" : qUnion([Q0]), "operationType" : NewBodyOperationType.REMOVE, "oppositeDirection" : true, "depth" : 3.58 * mm, "offsetDistance" : 25.4 * mm});
        }
        {
            var Q0;
            Q0=makeQuery(id+"F14.opExtrude","CAP_EDGE",EDGE,{"disambiguationData":[OSD([sQuery(id+"F13.wireOp",EDGE,"E10.right")])],"isStart":false});
            var Q1;
            Q1=makeQuery(id+"F14.opExtrude","CAP_EDGE",EDGE,{"disambiguationData":[OSD([sQuery(id+"F13.wireOp",EDGE,"E10.top")])],"isStart":false});
            var Q2;
            Q2=makeQuery(id+"F14.opExtrude","CAP_EDGE",EDGE,{"disambiguationData":[OSD([sQuery(id+"F13.wireOp",EDGE,"E10.bottom")])],"isStart":false});
            var Q3;
            Q3=makeQuery(id+"F14.opExtrude","CAP_EDGE",EDGE,{"disambiguationData":[OSD([sQuery(id+"F13.wireOp",EDGE,"E10.left")])],"isStart":false});
            chamfer(context, id + "F22", {"entities" : qUnion([Q0, Q1, Q2, Q3]), "width" : 1.02 * mm, "tangentPropagation" : true});
        }
    });
